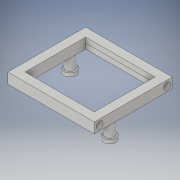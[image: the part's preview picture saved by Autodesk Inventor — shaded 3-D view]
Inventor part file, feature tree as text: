
AUTODESK INVENTOR PART (.ipt)
format: ipt  version: 2019 (Build 230136000, 136)  size: 148,992 bytes
history: native  units: in
note: dims shown in document units (in); Inventor stores cm internally (conversion verified against a paired STEP export)
features: sketch x5, extrude x4, hole x1
ambient origin geometry x8: Origin, YZ Plane, XZ Plane, XY Plane, X Axis, Y Axis, Z Axis, Center Point
bodies: Solid1 (feature_tree)
feature tree (10):
  extrude  "Extrusion1"  Depth=1.9685in
  extrude  "Extrusion2"  Depth=1.9685in
  sketch  "Sketch3"  dims[d9=1.378in d10=1.5748in]
  extrude  "Extrusion3"  Depth=1.5748in
  extrude  "Extrusion4"  Depth=0.2362in TaperAngle=0.0deg
  hole  "Hole2"  [1 undecoded]
  sketch  "Sketch1"  dims[d2=1.7717in d3=1.9685in]
  sketch  "Sketch2"  dims[d4=1.7717in d5=1.9685in]
  sketch  "Sketch4"  dims[d11=1.378in d12=0.2362in d13=0.0in]
  sketch  "Sketch6"  dims[d16=0.1969in d19=0.1969in d20=0.2953in d21=0.0in d22=0.2756in d23=0.2756in d24=0.0787in d25=0.0in d26=0.0787in d27=0.0in d41=0.2362in d44=0.1575in d45=0.1575in d46=0.1575in d47=0.2362in d48=0.1575in d49=0.0787in d50=90.0deg d51=0.315in d52=0.8108in d34=0.0394in d35=0.0394in d36=0.0394in d37=0.0059in d38=0.0098in d39=0.0148in d40=0.5635in d42=0.8108in d43=0.0025in]
note: 1 required parameter value undecoded (feature->parameter linkage not recoverable at this tier; creation-order binding heuristic only, values carry confidence <= 0.55)
